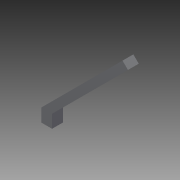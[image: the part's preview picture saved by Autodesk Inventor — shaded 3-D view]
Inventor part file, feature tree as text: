
AUTODESK INVENTOR PART (.ipt)
format: ipt  version: 2013 (Build 170138000, 138)  size: 71,168 bytes
history: native  units: in
note: dims shown in document units (in); Inventor stores cm internally (conversion verified against a paired STEP export)
features: extrude x1, sketch x1
ambient origin geometry x8: Origin, YZ Plane, XZ Plane, XY Plane, X Axis, Y Axis, Z Axis, Center Point
bodies: Solid1 (feature_tree)
feature tree (2):
  extrude  "Extrusion1"  Depth=0.25in
  sketch  "Sketch1"  dims[d1=0.3in d2=0.25in d3=0.3in d4=45.0deg d5=0.125in d6=0.125in d7=0.25in d8=0.0in]
